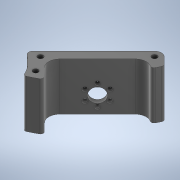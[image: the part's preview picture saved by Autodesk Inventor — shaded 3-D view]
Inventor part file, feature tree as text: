
AUTODESK INVENTOR PART (.ipt)
format: ipt  version: 2020 (Build 240168000, 168)  size: 689,152 bytes
history: native  units: mm
features: extrude x6, sketch x5, projected_geometry x2, other x1, chamfer x1, fillet x1
ambient origin geometry x8: Origin, YZ Plane, XZ Plane, XY Plane, X Axis, Y Axis, Z Axis, Center Point
bodies: Body1 (feature_tree)
feature tree (16):
  other  "Твердое тело1"
  sketch  "Эскиз1"
  extrude  "Выдавливание10"  Depth=3.8mm
  sketch  "Эскиз6"
  extrude  "Выдавливание13"  Depth=6.0mm
  extrude  "Выдавливание14"  Depth=35.0mm TaperAngle=0.0deg
  chamfer  "Фаска3"  Distance=59.0mm
  extrude  "Выдавливание15"  Depth=21.3mm
  fillet  "Сопряжение1"  Radius=15.0mm
  extrude  "Выдавливание16"  Depth=10.4mm
  extrude  "Выдавливание17"  Depth=2.5mm
  sketch  "Эскиз7"
  sketch  "Эскиз8"
  projected_geometry  "Спроецированная петля3"
  sketch  "Эскиз9"
  projected_geometry  "Спроецированная петля4"
